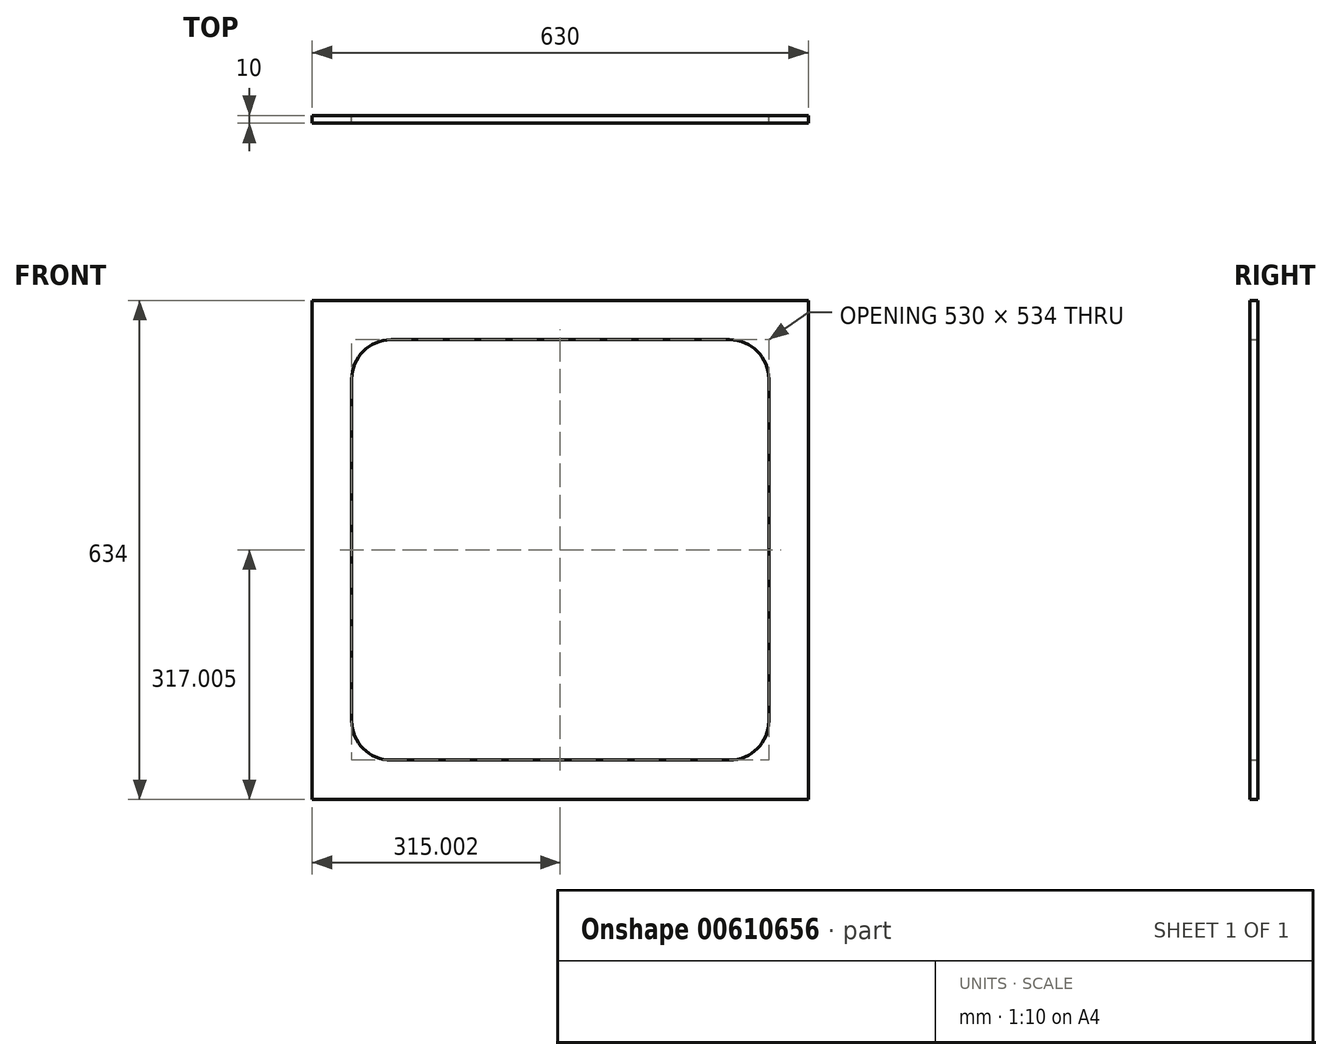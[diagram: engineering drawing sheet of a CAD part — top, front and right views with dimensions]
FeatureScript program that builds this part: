
annotation { "Feature Type Name" : "Feature", "Feature Type Description" : "" }
export const myFeature = defineFeature(function(context is Context, id is Id, definition is map)
    precondition{}
    {
        {
            var Q0;
            Q0=qCreatedBy(makeId("Front.planeOp"),FACE);
            var sketch = newSketch(context, id + "F0", { "sketchPlane" : qUnion([Q0])});
            skLineSegment(sketch, "E0.top", {"start": v(-341.35, -229.92) * mm, "end": v(288.65, -229.92) * mm});
            skLineSegment(sketch, "E1", {"start": v(-341.35, 404.08) * mm, "end": v(288.65, 404.08) * mm});
            skLineSegment(sketch, "E2", {"start": v(-341.35, 404.08) * mm, "end": v(-341.35, -229.92) * mm});
            skLineSegment(sketch, "E3", {"start": v(288.65, 404.08) * mm, "end": v(288.65, -229.92) * mm});
            skLineSegment(sketch, "E4", {"start": v(-241.35, 354.08) * mm, "end": v(188.65, 354.08) * mm});
            skLineSegment(sketch, "E5", {"start": v(-291.35, 304.08) * mm, "end": v(-291.35, -129.92) * mm});
            skLineSegment(sketch, "E6", {"start": v(-241.35, -179.92) * mm, "end": v(188.65, -179.92) * mm});
            skLineSegment(sketch, "E7", {"start": v(238.65, -129.92) * mm, "end": v(238.65, 304.08) * mm});
            skPoint(sketch, "E8.visualSharp", {"position": v(-291.35, 354.08) * mm});
            skArc(sketch, "E8.filletArc", {"start": v(-241.35, 354.08) * mm, "mid": v(-276.7, 339.44) * mm, "end": v(-291.35, 304.08) * mm});
            skPoint(sketch, "E9.visualSharp", {"position": v(238.65, 354.08) * mm});
            skArc(sketch, "E9.filletArc", {"start": v(238.65, 304.08) * mm, "mid": v(224, 339.44) * mm, "end": v(188.65, 354.08) * mm});
            skPoint(sketch, "E10.visualSharp", {"position": v(238.65, -179.92) * mm});
            skArc(sketch, "E10.filletArc", {"start": v(188.65, -179.92) * mm, "mid": v(224, -165.27) * mm, "end": v(238.65, -129.92) * mm});
            skPoint(sketch, "E11.visualSharp", {"position": v(-291.35, -179.92) * mm});
            skArc(sketch, "E11.filletArc", {"start": v(-291.35, -129.92) * mm, "mid": v(-276.7, -165.27) * mm, "end": v(-241.35, -179.92) * mm});
            skSolve(sketch);
        }
        {
            var Q0;
            Q0=makeQuery(id+"F0.imprint","IMPRINT",FACE,{"disambiguationData":[TD([[makeQuery(id+"F0.imprint","IMPRINT",EDGE,{"derivedFrom":sQuery(id+"F0.wireOp",EDGE,"E0.bottom")}),-1.0]])]});
            var Q1;
            Q1=makeQuery(id+"F0.imprint","IMPRINT",FACE,{"disambiguationData":[TD([[makeQuery(id+"F0.imprint","IMPRINT",EDGE,{"derivedFrom":sQuery(id+"F0.wireOp",EDGE,"E0.top")}),1.0]])]});
            extrude(context, id + "F1", {"entities" : qUnion([Q0, Q1]), "depth" : 10 * mm, "offsetDistance" : 25 * mm});
        }
    });
